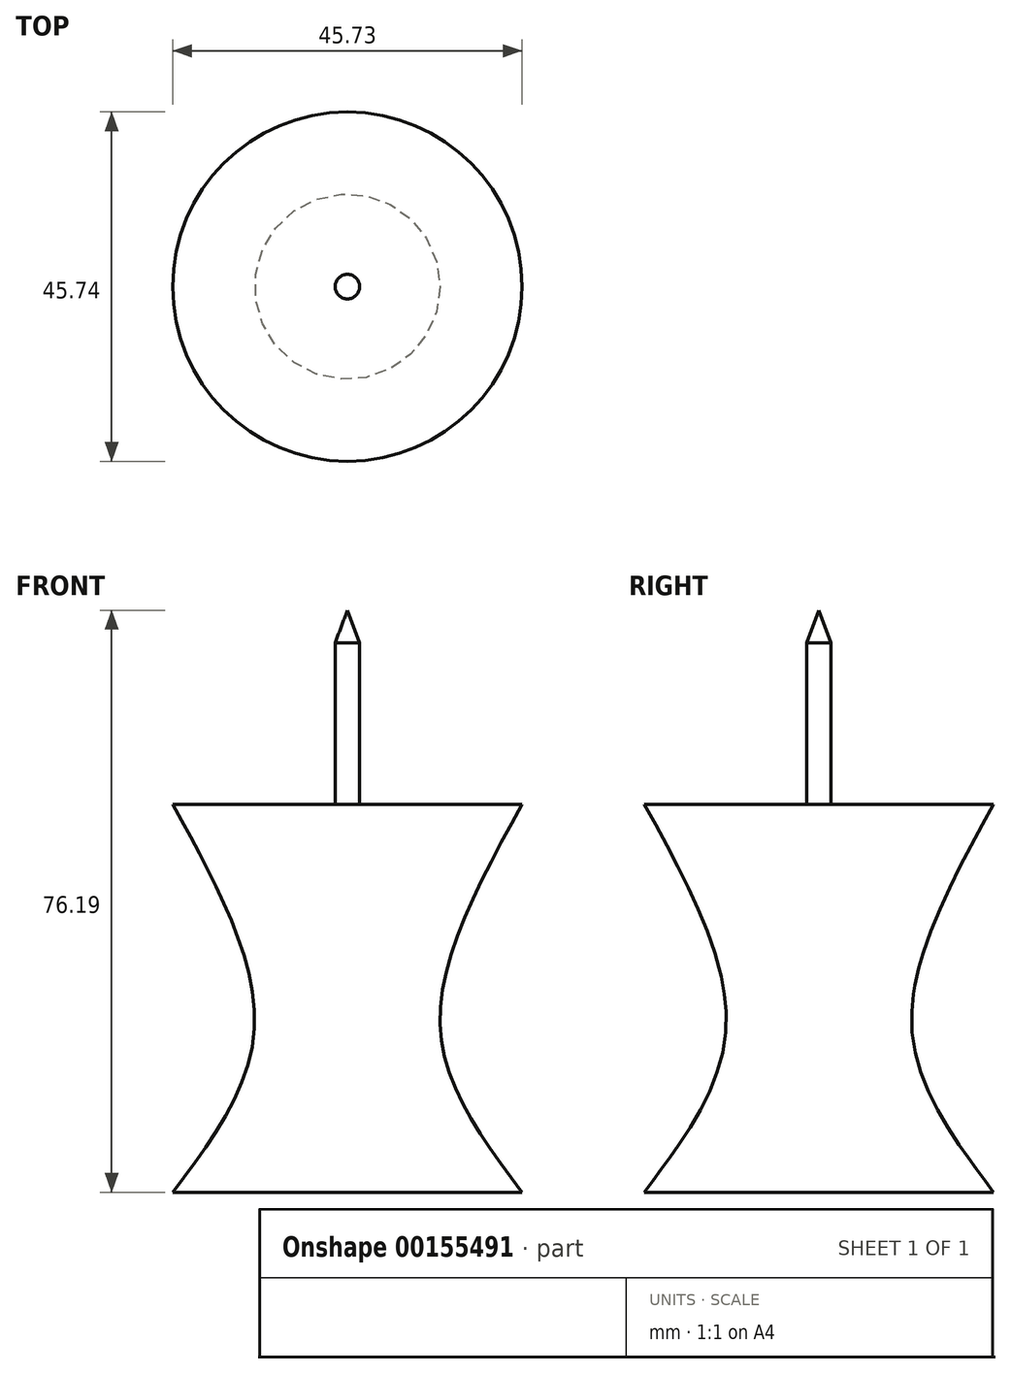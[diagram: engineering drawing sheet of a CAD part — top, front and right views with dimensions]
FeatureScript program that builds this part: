
annotation { "Feature Type Name" : "Feature", "Feature Type Description" : "" }
export const myFeature = defineFeature(function(context is Context, id is Id, definition is map)
    precondition{}
    {
        {
            var Q0;
            Q0=qCreatedBy(makeId("Front.planeOp"),FACE);
            var sketch = newSketch(context, id + "F0", { "sketchPlane" : qUnion([Q0])});
            skLineSegment(sketch, "E0", {"start": v(-33.73, -35.65) * mm, "end": v(-10.88, -35.65) * mm});
            skFitSpline(sketch, "E1", {"points": [v(-10.88, 15.14) * mm, v(-21.56, -14.19) * mm, v(-10.88, -35.65) * mm], "startDerivative": vector(-31.46, -57.37) * mm, "endDerivative": vector(32.97, -42.87) * mm});
            skLineSegment(sketch, "E2", {"start": v(-33.73, 40.54) * mm, "end": v(-32.12, 36.27) * mm});
            skLineSegment(sketch, "E3", {"start": v(-32.12, 36.27) * mm, "end": v(-32.12, 15.14) * mm});
            skLineSegment(sketch, "E4", {"start": v(-33.73, 40.54) * mm, "end": v(-33.73, -35.65) * mm});
            skLineSegment(sketch, "E5", {"start": v(-33.73, -35.65) * mm, "end": v(-56.6, -35.65) * mm});
            skLineSegment(sketch, "E6", {"start": v(-35.33, 36.27) * mm, "end": v(-33.73, 40.54) * mm});
            skLineSegment(sketch, "E7", {"start": v(-35.33, 36.27) * mm, "end": v(-35.33, 15.14) * mm});
            skFitSpline(sketch, "E8", {"points": [v(-56.6, 15.14) * mm, v(-45.89, -14.19) * mm, v(-56.6, -35.65) * mm], "startDerivative": vector(31.55, -57.44) * mm, "endDerivative": vector(-32.97, -43.83) * mm});
            skLineSegment(sketch, "E9", {"start": v(-56.6, 15.14) * mm, "end": v(-35.33, 15.14) * mm});
            skLineSegment(sketch, "E10", {"start": v(-10.88, 15.14) * mm, "end": v(-32.12, 15.14) * mm});
            skSolve(sketch);
        }
        {
            var Q0;
            Q0=makeQuery(id+"F0.imprint","IMPRINT",FACE,{"disambiguationData":[TD([[makeQuery(id+"F0.imprint","IMPRINT",EDGE,{"derivedFrom":sQuery(id+"F0.wireOp",EDGE,"E4")}),-1.0]])]});
            var Q1;
            Q1=sQuery(id+"F0.wireOp",EDGE,"E4");
            revolve(context, id + "F1", {"entities" : qUnion([Q0]), "axis" : qUnion([Q1]), "revolveType" : RevolveType.FULL});
        }
    });
